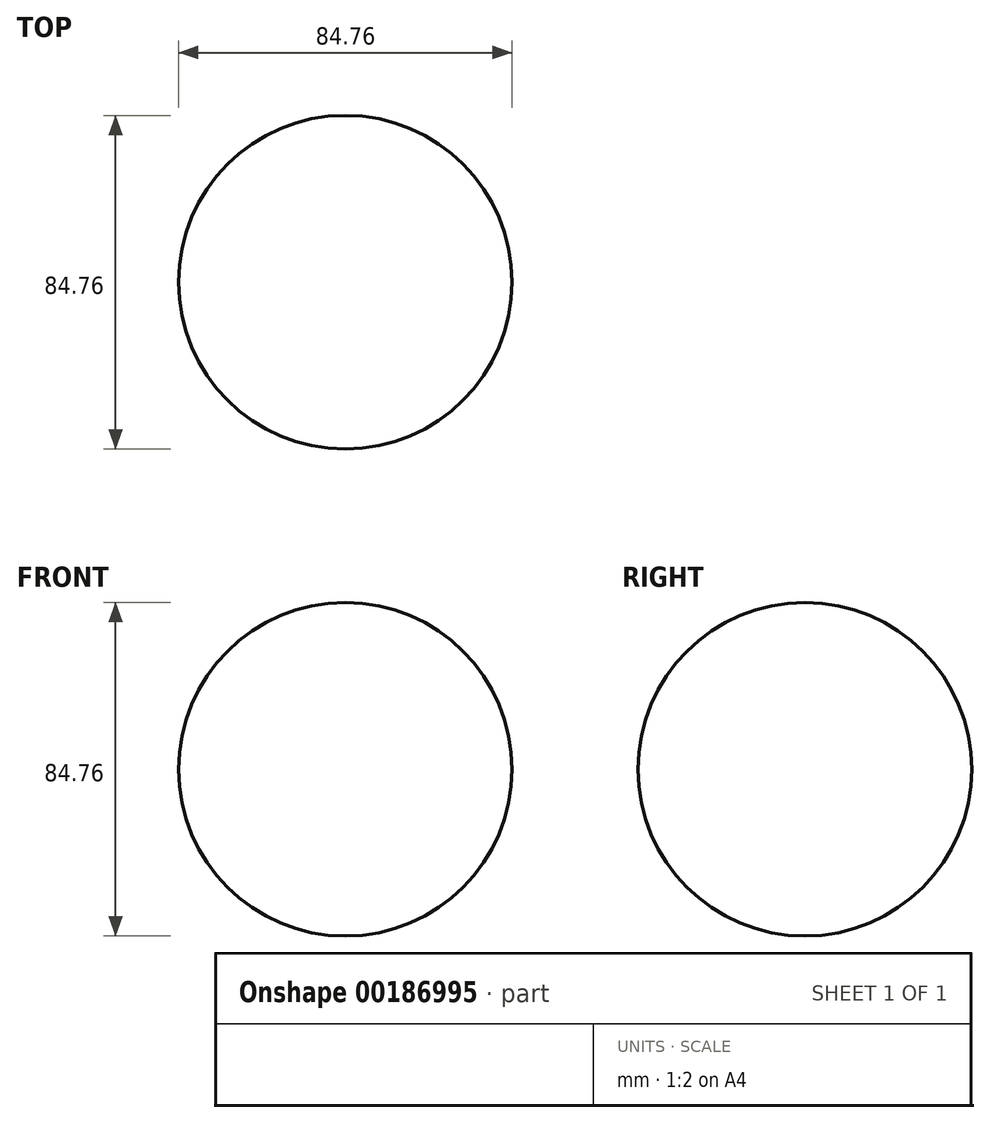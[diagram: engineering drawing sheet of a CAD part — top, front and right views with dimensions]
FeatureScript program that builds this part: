
annotation { "Feature Type Name" : "Feature", "Feature Type Description" : "" }
export const myFeature = defineFeature(function(context is Context, id is Id, definition is map)
    precondition{}
    {
        {
            var Q0;
            Q0=qCreatedBy(makeId("Front.planeOp"),FACE);
            var sketch = newSketch(context, id + "F0", { "sketchPlane" : qUnion([Q0])});
            skCircle(sketch, "E0", {"center": v(0, 0) * mm, "radius": 42.38 * mm});
            skLineSegment(sketch, "E1", {"start": v(0, 42.38) * mm, "end": v(0, -42.38) * mm});
            skSolve(sketch);
        }
        {
            var Q0;
            {var subQ0=sQuery(id+"F0.wireOp",EDGE,"E1");Q0=makeQuery(id+"F0.imprint","IMPRINT",FACE,{"disambiguationData":[TD([[makeQuery(id+"F0.imprint","IMPRINT",EDGE,{"derivedFrom":subQ0}),-1.0]])]});}
            var Q1;
            Q1=sQuery(id+"F0.wireOp",EDGE,"E1");
            revolve(context, id + "F1", {"entities" : qUnion([Q0]), "axis" : qUnion([Q1]), "revolveType" : RevolveType.FULL});
        }
    });
